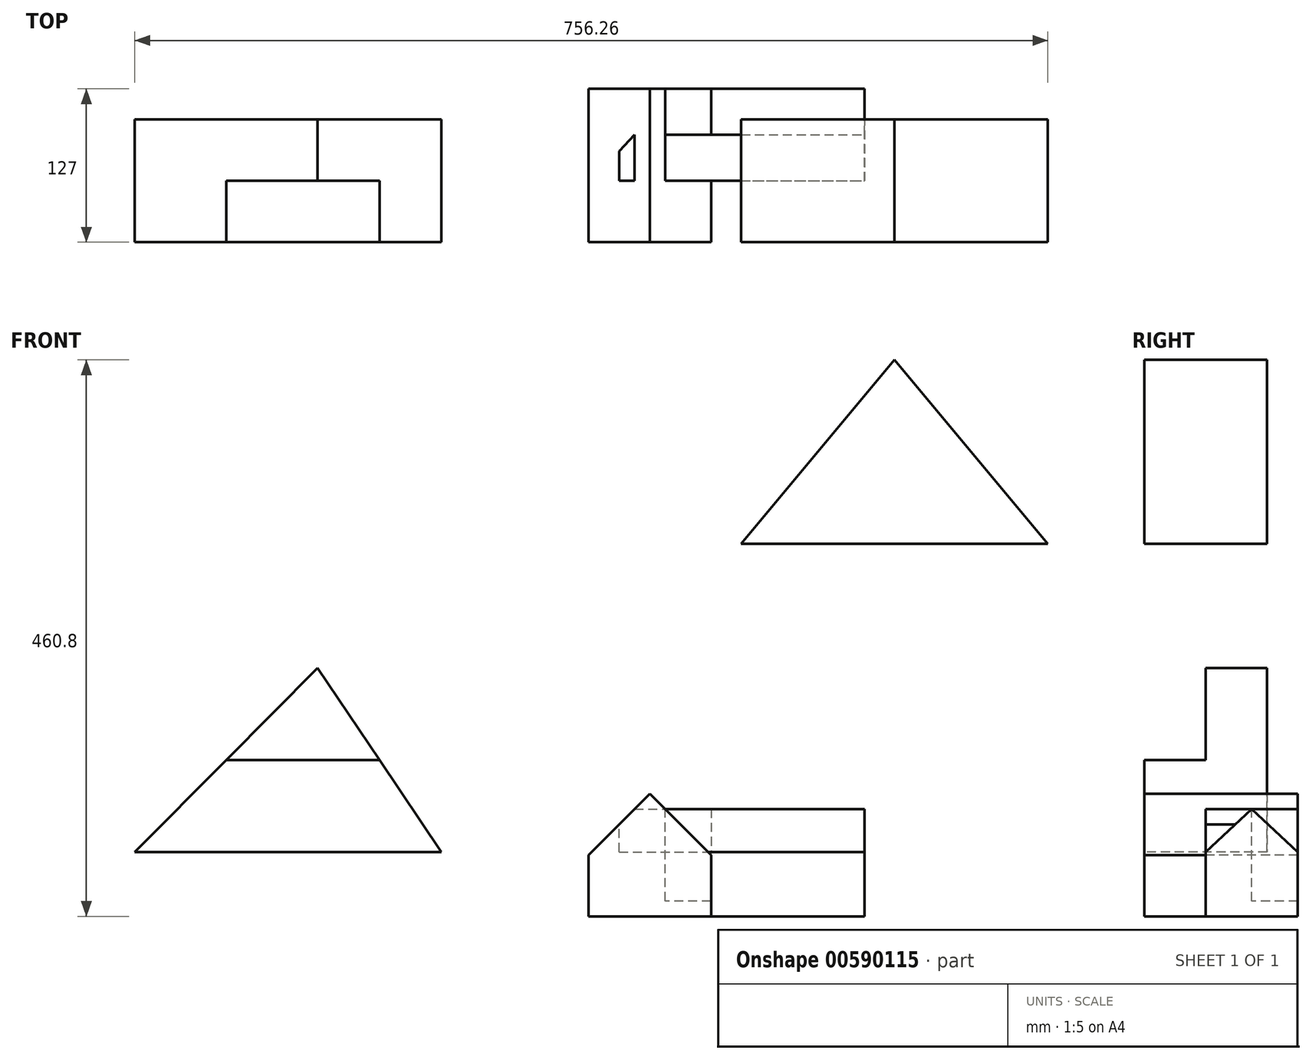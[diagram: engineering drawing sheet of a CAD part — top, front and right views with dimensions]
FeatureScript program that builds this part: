
annotation { "Feature Type Name" : "Feature", "Feature Type Description" : "" }
export const myFeature = defineFeature(function(context is Context, id is Id, definition is map)
    precondition{}
    {
        {
            var Q0;
            Q0=qCreatedBy(makeId("Front.planeOp"),FACE);
            var sketch = newSketch(context, id + "F0", { "sketchPlane" : qUnion([Q0])});
            skLineSegment(sketch, "E0", {"start": v(0, -152.4) * mm, "end": v(-254, -152.4) * mm});
            skLineSegment(sketch, "E1", {"start": v(-254, -152.4) * mm, "end": v(-102.51, 0) * mm});
            skLineSegment(sketch, "E2", {"start": v(-102.51, 0) * mm, "end": v(0, -152.4) * mm});
            skLineSegment(sketch, "E3", {"start": v(-178.26, -76.2) * mm, "end": v(-51.26, -76.2) * mm});
            skSolve(sketch);
        }
        {
            var Q0;
            {var subQ0=sQuery(id+"F0.wireOp",EDGE,"E0");Q0=makeQuery(id+"F0.imprint","IMPRINT",FACE,{"disambiguationData":[TD([[makeQuery(id+"F0.imprint","IMPRINT",EDGE,{"derivedFrom":subQ0}),-1.0]])]});}
            var Q1;
            {var subQ3=sQuery(id+"F0.wireOp",EDGE,"E3");Q1=makeQuery(id+"F0.imprint","IMPRINT",FACE,{"disambiguationData":[TD([[makeQuery(id+"F0.imprint","IMPRINT",EDGE,{"derivedFrom":subQ3}),1.0]])]});}
            extrude(context, id + "F1", {"entities" : qUnion([Q0, Q1]), "oppositeDirection" : true, "depth" : 101.6 * mm, "offsetDistance" : 25.4 * mm});
        }
        {
            var Q0;
            Q0=makeQuery(id+"F1.opExtrude","CAP_FACE",FACE,{"disambiguationData":[OSD([sQuery(id+"F0.wireOp",EDGE,"E0"),sQuery(id+"F0.wireOp",EDGE,"E1"),sQuery(id+"F0.wireOp",EDGE,"E2")])],"isStart":true});
            var sketch = newSketch(context, id + "F2", { "sketchPlane" : qUnion([Q0])});
            skLineSegment(sketch, "E4", {"start": v(-178.26, -76.2) * mm, "end": v(-51.26, -76.2) * mm});
            skLineSegment(sketch, "E5", {"start": v(-51.26, -76.2) * mm, "end": v(-102.51, 0) * mm});
            skLineSegment(sketch, "E6", {"start": v(-102.51, 0) * mm, "end": v(-178.26, -76.2) * mm});
            skSolve(sketch);
        }
        {
            var Q0;
            Q0=makeQuery(id+"F2.imprint","IMPRINT",FACE,{"disambiguationData":[TD([[makeQuery(id+"F2.imprint","IMPRINT",EDGE,{"derivedFrom":sQuery(id+"F2.wireOp",EDGE,"E4")}),1.0]])]});
            extrude(context, id + "F3", {"entities" : qUnion([Q0]), "operationType" : NewBodyOperationType.REMOVE, "oppositeDirection" : true, "depth" : 50.8 * mm, "offsetDistance" : 25.4 * mm});
        }
        {
            var Q0;
            Q0=qCreatedBy(makeId("Front.planeOp"),FACE);
            var sketch = newSketch(context, id + "F4", { "sketchPlane" : qUnion([Q0])});
            skLineSegment(sketch, "E7", {"start": v(248.26, 102.9) * mm, "end": v(502.26, 102.9) * mm});
            skLineSegment(sketch, "E8", {"start": v(375.26, 102.9) * mm, "end": v(375.26, 255.3) * mm});
            skLineSegment(sketch, "E9", {"start": v(502.26, 102.9) * mm, "end": v(375.26, 255.3) * mm});
            skLineSegment(sketch, "E10", {"start": v(248.26, 102.9) * mm, "end": v(375.26, 255.3) * mm});
            skSolve(sketch);
        }
        {
            var Q0;
            {var subQ2=sQuery(id+"F4.wireOp",EDGE,"E8");Q0=makeQuery(id+"F4.imprint","IMPRINT",FACE,{"disambiguationData":[TD([[makeQuery(id+"F4.imprint","IMPRINT",EDGE,{"derivedFrom":subQ2}),1.0]])]});}
            var Q1;
            {var subQ2=sQuery(id+"F4.wireOp",EDGE,"E8");Q1=makeQuery(id+"F4.imprint","IMPRINT",FACE,{"disambiguationData":[TD([[makeQuery(id+"F4.imprint","IMPRINT",EDGE,{"derivedFrom":subQ2}),-1.0]])]});}
            extrude(context, id + "F5", {"entities" : qUnion([Q0, Q1]), "oppositeDirection" : true, "depth" : 101.6 * mm, "offsetDistance" : 25.4 * mm});
        }
        {
            var Q0;
            Q0=qCreatedBy(makeId("Front.planeOp"),FACE);
            var sketch = newSketch(context, id + "F6", { "sketchPlane" : qUnion([Q0])});
            skLineSegment(sketch, "E11", {"start": v(350.29, -205.5) * mm, "end": v(350.29, -116.6) * mm});
            skLineSegment(sketch, "E12", {"start": v(121.69, -205.5) * mm, "end": v(350.29, -205.5) * mm});
            skLineSegment(sketch, "E13", {"start": v(121.69, -205.5) * mm, "end": v(121.69, -154.7) * mm});
            skLineSegment(sketch, "E14", {"start": v(223.29, -154.7) * mm, "end": v(223.29, -205.5) * mm});
            skLineSegment(sketch, "E15", {"start": v(223.29, -154.7) * mm, "end": v(350.29, -154.7) * mm});
            skLineSegment(sketch, "E16", {"start": v(172.49, -103.9) * mm, "end": v(121.69, -154.7) * mm});
            skLineSegment(sketch, "E17", {"start": v(172.49, -103.9) * mm, "end": v(223.29, -154.7) * mm});
            skLineSegment(sketch, "E18", {"start": v(350.29, -116.6) * mm, "end": v(185.19, -116.6) * mm});
            skSolve(sketch);
        }
        {
            var Q0;
            {var subQ1=sQuery(id+"F6.wireOp",EDGE,"E13");Q0=makeQuery(id+"F6.imprint","IMPRINT",FACE,{"disambiguationData":[TD([[makeQuery(id+"F6.imprint","IMPRINT",EDGE,{"derivedFrom":subQ1}),-1.0]])]});}
            var Q1;
            {var subQ2=sQuery(id+"F6.wireOp",EDGE,"E15");Q1=makeQuery(id+"F6.imprint","IMPRINT",FACE,{"disambiguationData":[TD([[makeQuery(id+"F6.imprint","IMPRINT",EDGE,{"derivedFrom":subQ2}),1.0]])]});}
            var Q2;
            {var subQ4=sQuery(id+"F6.wireOp",EDGE,"E14");Q2=makeQuery(id+"F6.imprint","IMPRINT",FACE,{"disambiguationData":[TD([[makeQuery(id+"F6.imprint","IMPRINT",EDGE,{"derivedFrom":subQ4}),1.0]])]});}
            extrude(context, id + "F7", {"entities" : qUnion([Q0, Q1, Q2]), "oppositeDirection" : true, "depth" : 127 * mm, "offsetDistance" : 25.4 * mm});
        }
        {
            var Q0;
            {var subQ4=sQuery(id+"F6.wireOp",EDGE,"E14");Q0=makeQuery(id+"F6.imprint","IMPRINT",FACE,{"disambiguationData":[TD([[makeQuery(id+"F6.imprint","IMPRINT",EDGE,{"derivedFrom":subQ4}),1.0]])]});}
            extrude(context, id + "F8", {"entities" : qUnion([Q0]), "operationType" : NewBodyOperationType.REMOVE, "oppositeDirection" : true, "depth" : 50.8 * mm, "offsetDistance" : 25.4 * mm});
        }
        {
            var Q0;
            {var subQ2=sQuery(id+"F6.wireOp",EDGE,"E15");Q0=makeQuery(id+"F6.imprint","IMPRINT",FACE,{"disambiguationData":[TD([[makeQuery(id+"F6.imprint","IMPRINT",EDGE,{"derivedFrom":subQ2}),1.0]])]});}
            extrude(context, id + "F9", {"entities" : qUnion([Q0]), "operationType" : NewBodyOperationType.REMOVE, "oppositeDirection" : true, "depth" : 50.8 * mm, "offsetDistance" : 25.4 * mm});
        }
        {
            var Q0;
            Q0=makeQuery(id+"F7.opExtrude","SWEPT_FACE",FACE,{"disambiguationData":[OSD([sQuery(id+"F6.wireOp",EDGE,"E11")])]});
            var sketch = newSketch(context, id + "F10", { "sketchPlane" : qUnion([Q0])});
            skLineSegment(sketch, "E19", {"start": v(50.8, -152.12) * mm, "end": v(88.9, -116.6) * mm});
            skLineSegment(sketch, "E20", {"start": v(88.9, -116.6) * mm, "end": v(127, -152.12) * mm});
            skSolve(sketch);
        }
        {
            var Q0;
            {var subQ0=sQuery(id+"F10.wireOp",EDGE,"E19");Q0=makeQuery(id+"F10.imprint","IMPRINT",FACE,{"disambiguationData":[TD([[makeQuery(id+"F10.imprint","IMPRINT",EDGE,{"derivedFrom":subQ0}),1.0]])]});}
            var Q1;
            {var subQ0=sQuery(id+"F10.wireOp",EDGE,"E20");Q1=makeQuery(id+"F10.imprint","IMPRINT",FACE,{"disambiguationData":[TD([[makeQuery(id+"F10.imprint","IMPRINT",EDGE,{"derivedFrom":subQ0}),1.0]])]});}
            extrude(context, id + "F11", {"entities" : qUnion([Q0, Q1]), "operationType" : NewBodyOperationType.REMOVE, "oppositeDirection" : true, "depth" : 127 * mm, "offsetDistance" : 25.4 * mm});
        }
        {
            var Q0;
            Q0=makeQuery(id+"F11.boolean.opBoolean","COPY",FACE,{"derivedFrom":makeQuery(id+"F11.opExtrude","CAP_FACE",FACE,{"disambiguationData":[OSD([sQuery(id+"F6.wireOp",EDGE,"E11"),sQuery(id+"F6.wireOp",EDGE,"E18"),sQuery(id+"F10.wireOp",EDGE,"E19")])],"isStart":false})});
            extrude(context, id + "F12", {"entities" : qUnion([Q0]), "operationType" : NewBodyOperationType.REMOVE, "oppositeDirection" : true, "depth" : 50.8 * mm, "offsetDistance" : 25.4 * mm});
        }
        {
            var Q0;
            Q0=makeQuery(id+"F12.boolean.opBoolean","COPY",FACE,{"derivedFrom":makeQuery(id+"F12.opExtrude","CAP_FACE",FACE,{"disambiguationData":[OSD([sQuery(id+"F6.wireOp",EDGE,"E11"),sQuery(id+"F6.wireOp",EDGE,"E18"),sQuery(id+"F10.wireOp",EDGE,"E19")])],"isStart":false})});
            extrude(context, id + "F13", {"entities" : qUnion([Q0]), "operationType" : NewBodyOperationType.REMOVE, "oppositeDirection" : true, "depth" : 25.4 * mm, "offsetDistance" : 25.4 * mm});
        }
        {
            var Q0;
            Q0=makeQuery(id+"F7.opExtrude","SWEPT_FACE",FACE,{"disambiguationData":[OSD([sQuery(id+"F6.wireOp",EDGE,"E18")])]});
            extrude(context, id + "F14", {"entities" : qUnion([Q0]), "operationType" : NewBodyOperationType.REMOVE, "oppositeDirection" : true, "depth" : 76.2 * mm, "offsetDistance" : 25.4 * mm});
        }
    });
